# Revit family: PRD_FrankeWS_WshTrghs_SaturnWashTrough_SOLX1200,1200T,1800,1800T
name_source: partatom
category: Plumbing Fixtures
revit_build: Autodesk Revit 2018 (Build: 20190510_1515(x64)
units: mm (PartAtom-declared; Revit-internal decimal feet)

## family parameters
Cut with Voids When Loaded = No
Host = Face
OmniClass Number = 23.45.05.14.14
OmniClass Title = Sinks/Lavatories
Part Type = Normal
Room Calculation Point = No
Round Connector Dimension = Use Diameter
Shared = No

## types (4) — shared parameters
AssetType = Fixed
Category = Pr_40_20_96_99, Wash troughs
Color = Alpine white
Default Elevation = 850 mm  [stored 2.78871 ft]
DrainSize = DN 32 (1 1/4 inch.)
DurationUnit = year
Form = Wall mounted
IfcExportAs = IfcSanitaryTerminalType
IfcExportType = WASHHANDBASIN
IntegralAccessories = Screws and dowels
Manufacturer = KWC Group AG
ManufacturerName = KWC Group AG
ManufacturerURL = www.kwc.com
Material = MIRANIT
MaterialsBody = Miranit
MaterialsFinishAndColour = Alpine white
NBSDescription = Wash troughs
NBSReference = 45-35-70/370
NominalDepth = 170 mm  [stored 0.557743 ft]
NominalHeight = 170 mm  [stored 0.557743 ft]
NominalLength = 480 mm  [stored 1.5748 ft]
ProductInformation = https://pim.kwc.com
URL = www.kwc.com
Uniclass2015Code = Pr_40_20_96_99
Uniclass2015Title = Wash troughs
Uniclass2015Version = Products v1.10
Version = 1
WarrantyDurationUnit = year
WashHandBasinMounting = WallHung
WashHandBasinType = WashingTrough
WashbasinMaterial = PRD_AR_Miranit_Alpinewhite
WasteSize = 32  [stored 0.104987 ft]
WaterSupplyOverflowAndWasteHolesOverflow = yes
WaterSupplyOverflowAndWasteHolesWaste = CENTER-BACK

## per-type parameters (varying)
| type | BIMObjectName | Description | Features | GrossWeight | ModelNumber | Name | NetWeight | NominalWidth | Size | Station | TapholesSOLX1200T | TapholesSOLX1800T | WaterSupplyOverflowAndWasteHolesWaterSupply | type |
| SOLX1800T | PRD_AR_WashTrough_Saturn_SOLX1800T | 3 person washtrough. Made of Miranit resin-bonded mineral composite, with pore-free, smooth gelcoat high-polished surface (temperature-resistant up to 80°C). Include a 32 mm waste kit with overflow. CE Certified. Colour Alpine white. With tap holes. Dimensions 1800 x 480 x 170 mm (W x H x D) | Mineral material, with 3 tapholes, wall mounting, 1800x170x480 mm (WxHxD). | 36 | 2030010646 | SATURN Wash troughs SOLX1800T | 36 | 1800 mm  [stored 5.90551 ft] | 1800 x 170 x 480 mm | 3 | No | Yes | 3 tapholes | SOLX1800 |
| SOLX1200T | PRD_AR_WashTrough_Saturn_SOLX1200T | 2 person washtrough. Made of Miranit resin-bonded mineral composite, with pore-free, smooth gelcoat high-polished surface (temperature-resistant up to 80°C). Include a 32 mm waste kit with overflow.
CE Certified
Colour Alpine white
With tap holes
Dimensions 1200 x 480 x 170 mm (W x H x D) | Mineral material, with 2 tapholes, wall mounting, 1200x170x480 mm (WxHxD). | 36 | 2030010640 | SATURN Wash troughs SOLX1200T | 36 | 1200 mm | 1200 x 170 x 480 mm | 2 | Yes | No | 2 tapholes | SOLX1200 |
| SOLX1200 | PRD_AR_WashTrough_Saturn_SOLX1200 | Washtrough made from Miranit resin bonded mineral material, with an alpine white gelcoat surface finish that's smooth, pore-free and temperature resistant up to 80°C. Washtroughs include a 32mm waste kit with overflow. Available with or without splashback, there is also a choice of either self-closing or electronic, touch free taps. CE Certified. No Tap holes (tap drill points marked underneath) with overflow, colour: Alpine white. 2 wash places dimensions: 1200 x 480 x 170mm | Mineral material, wall mounting, 1200x170x480 mm (WxHxD). | 37 | 2030005452 | SATURN Wash troughs SOLX1200 | 36 | 1800 mm  [stored 5.90551 ft] | 1200 x 170 x 480 mm | 2 | No | No | no tapholes | SOLX1200 |
| SOLX1800 | PRD_AR_WashTrough_Saturn_SOLX1800 | Washtrough made from Miranit resin bonded mineral material, with an alpine white gelcoat surface finish that's smooth, pore-free and temperature resistant up to 80°C. Washtroughs include a 32mm waste kit with overflow. Available with or without splashback, there is also a choice of either self-closing or electronic, touch free taps. CE Certified. No Tap holes (tap drill points marked underneath) with overflow, colour: Alpine white. 3 wash places dimensions: 1800 x 480 x 170mm | Mineral material, wall mounting, 1800x170x480 mm (WxHxD). | 46 | 2030005465 | SATURN Wash troughs SOLX1800 | 46 | 1800 mm  [stored 5.90551 ft] | 1800 x 170 x 480 mm | 3 | No | No | no tapholes | SOLX1800 |

note: column(s) folded — value = type name in every type: Model, ModelReference

note: [stored X ft] marks values corroborated as IEEE doubles in the binary element streams (Revit-internal decimal feet)

## geometry (parser evidence)
native form markers: Sweep x6
no freeform markers — native parametric forms only
